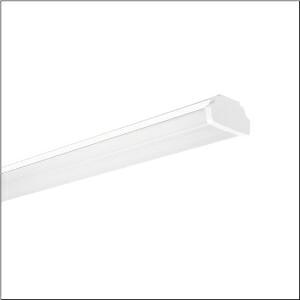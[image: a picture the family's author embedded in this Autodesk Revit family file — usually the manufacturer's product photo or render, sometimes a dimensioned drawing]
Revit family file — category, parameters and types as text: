
# Revit family: modario_r__31_ho_53bm811m1v4120_5d14
name_source: partatom
category: Lighting Fixtures
units: mm (PartAtom-declared; Revit-internal decimal feet)

## family parameters
Cut with Voids When Loaded = No
Host = Face
Light Source = No
Part Type = Normal
Room Calculation Point = No
Round Connector Dimension = Use Diameter
Shared = No

## types (1)
- --- (1 x LED, 12380 lm, 77.3 W, 4000K)
    Apparent Load = 77 VA
    CIE Flux Codes = 52 78 94 90 100
    Color Rendering = 80
    Color Temperature = 4000K
    Default Elevation = 1800 mm
    Description = Modario® 31 HO, luminaire insert, of sheet steel, coil coated, white, length: 1.495mm, width: 81mm, height: 82mm, 5x system unit, system units: 299mm, LED rated luminous flux: 12.380lm, light colour: 840, control gear: ON/OFF Multilumen, control gear: ECG Multilumen, with plug, 3-pole, with phase selection, mains connection: 220..240V, AC, 50/60Hz, rated input power: 77W, through-wiring accessed according to module size, primary optical cover: cover, of PMMA, light emission: direct distribution, primary light characteristic: symmetric, protection rating (complete): IP20, protection rating (LED compartment): IP50, insulation class (complete): insulation class I (protective earthing), certification: CE, ENEC, VDE, UKCA, impact resistance: IK03, permissible ambient temperature for indoor applications: -35..+35°C, corresponds to IFS (International Featured Standards) requirements for safety and quality in the food industry, reducing of maximum allowable ambient temperature of 5°C with ceiling mounting, packaging unit: 1 piece
    Height = 92 mm
    Lamp = 1 x LED
    Lamp Light Flux = 12380 lm
    Lamp Power = 77.3 W
    Lamp count = 1
    Length = 1495 mm
    Luminous efficacy = 160 lm/W
    Manufacturer = Siteco
    ModVariant = No
    Model = 53BM811M1V4120
    Mounting Place = Ceiling
    Mounting Type = Pendant
    Number of Poles = 1
    OnlyDefault = Yes
    Power Factor = 1
    Product Name = Modario® 31 HO
    Product group = luminaire insert
    ProductGroupID = 901
    Protection Class = Protection class I
    Protection Degree = IP 20
    RLX_Detail_Level = 1
    RLX_Emergency_Light_Flux = 0 lm
    RLX_Emergency_Type = 0
    RLX_Emergency_Type_DB = No
    RlxData = <blob elided: 40281 chars, md5=33172e7d>
    Socket = socket
    Standby Power = 0 W
    System Light Flux = 12380 lm
    System Power = 77 W
    Type Comments = factory setting: luminous flux: 100 % | (A | C | E) | 173 mA
    Type Image = l_1300283.jpg
    URL = http://relux.com
    VarID = @adj_152509
    Voltage = 0 V
    Weight = 0.00 kg
    Width = 81 mm

## geometry (parser evidence)
native form markers: Blend x4, Sweep x12
no freeform markers — native parametric forms only
